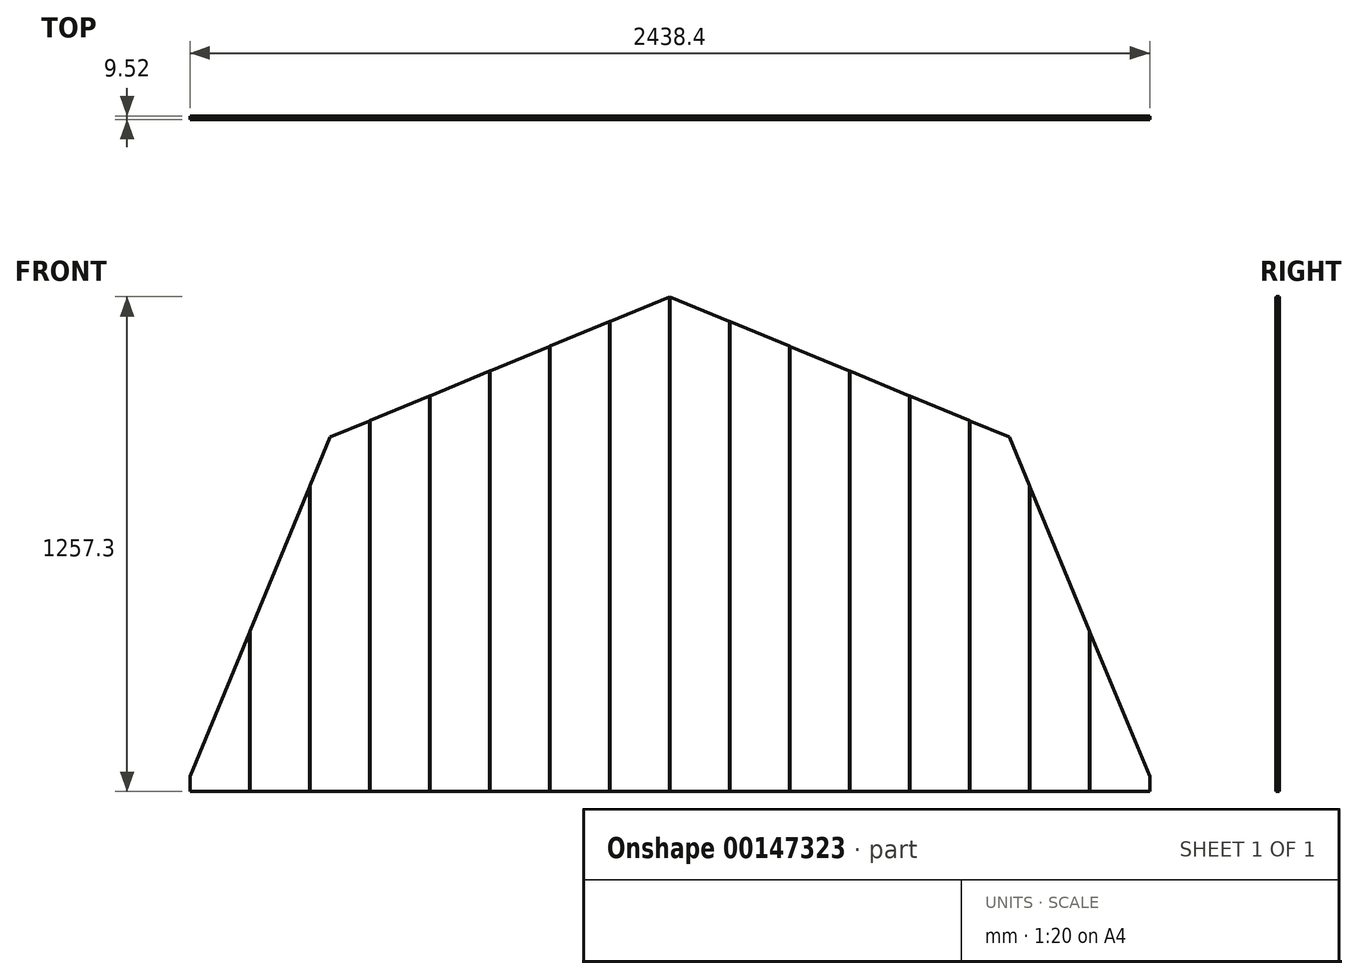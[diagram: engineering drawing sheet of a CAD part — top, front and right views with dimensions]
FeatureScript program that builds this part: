
annotation { "Feature Type Name" : "Feature", "Feature Type Description" : "" }
export const myFeature = defineFeature(function(context is Context, id is Id, definition is map)
    precondition{}
    {
        {
            var Q0;
            Q0=qCreatedBy(makeId("Front.planeOp"),FACE);
            var sketch = newSketch(context, id + "F0", { "sketchPlane" : qUnion([Q0])});
            skLineSegment(sketch, "E0", {"start": v(-1027.18, -196.14) * mm, "end": v(-670.66, 666.55) * mm});
            skLineSegment(sketch, "E1", {"start": v(-670.66, 666.55) * mm, "end": v(192.02, 1023.06) * mm});
            skLineSegment(sketch, "E2.MirrorCS", {"start": v(1411.22, -196.14) * mm, "end": v(1054.7, 666.55) * mm});
            skLineSegment(sketch, "E3.MirrorCS", {"start": v(1054.7, 666.55) * mm, "end": v(192.02, 1023.06) * mm});
            skLineSegment(sketch, "E4.top", {"start": v(-1027.18, -234.24) * mm, "end": v(1411.22, -234.24) * mm});
            skLineSegment(sketch, "E4.left", {"start": v(-1027.18, -196.14) * mm, "end": v(-1027.18, -234.24) * mm});
            skLineSegment(sketch, "E4.right", {"start": v(1411.22, -196.14) * mm, "end": v(1411.22, -234.24) * mm});
            skSolve(sketch);
        }
        {
            var Q0;
            Q0=qSketchRegion(id+"F0",true);
            extrude(context, id + "F1", {"entities" : qUnion([Q0]), "endBound" : BoundingType.SYMMETRIC, "depth" : 9.52 * mm});
        }
        {
            var Q0;
            Q0=makeQuery(id+"F1.opExtrude","SWEPT_FACE",FACE,{"disambiguationData":[OSD([sQuery(id+"F0.wireOp",EDGE,"E4.top")])]});
            var sketch = newSketch(context, id + "F2", { "sketchPlane" : qUnion([Q0])});
            skLineSegment(sketch, "E5.bottom", {"start": v(-875.57, 4.76) * mm, "end": v(-873.98, 4.76) * mm});
            skLineSegment(sketch, "E5.top", {"start": v(-875.57, 3.17) * mm, "end": v(-873.98, 3.17) * mm});
            skLineSegment(sketch, "E5.left", {"start": v(-875.57, 4.76) * mm, "end": v(-875.57, 3.17) * mm});
            skLineSegment(sketch, "E5.right", {"start": v(-873.98, 4.76) * mm, "end": v(-873.98, 3.17) * mm});
            skPoint(sketch, "E6.end.orphan", {"position": v(-874.78, 4.76) * mm});
            skPoint(sketch, "E6.start.orphan", {"position": v(-874.78, 3.17) * mm});
            skPoint(sketch, "E7.1.0.0", {"position": v(-722.38, 3.17) * mm});
            skPoint(sketch, "E7.1.0.1", {"position": v(-722.38, 4.76) * mm});
            skLineSegment(sketch, "E7.1.0.2", {"start": v(-723.17, 4.76) * mm, "end": v(-721.58, 4.76) * mm});
            skLineSegment(sketch, "E7.1.0.3", {"start": v(-723.17, 3.17) * mm, "end": v(-721.58, 3.17) * mm});
            skLineSegment(sketch, "E7.1.0.4", {"start": v(-723.17, 4.76) * mm, "end": v(-723.17, 3.17) * mm});
            skLineSegment(sketch, "E7.1.0.5", {"start": v(-721.58, 4.76) * mm, "end": v(-721.58, 3.17) * mm});
            skPoint(sketch, "E7.2.0.0", {"position": v(-569.98, 3.17) * mm});
            skPoint(sketch, "E7.2.0.1", {"position": v(-569.98, 4.76) * mm});
            skLineSegment(sketch, "E7.2.0.2", {"start": v(-570.77, 4.76) * mm, "end": v(-569.18, 4.76) * mm});
            skLineSegment(sketch, "E7.2.0.3", {"start": v(-570.77, 3.17) * mm, "end": v(-569.18, 3.17) * mm});
            skLineSegment(sketch, "E7.2.0.4", {"start": v(-570.77, 4.76) * mm, "end": v(-570.77, 3.17) * mm});
            skLineSegment(sketch, "E7.2.0.5", {"start": v(-569.18, 4.76) * mm, "end": v(-569.18, 3.17) * mm});
            skPoint(sketch, "E7.3.0.0", {"position": v(-417.58, 3.17) * mm});
            skPoint(sketch, "E7.3.0.1", {"position": v(-417.58, 4.76) * mm});
            skLineSegment(sketch, "E7.3.0.2", {"start": v(-418.37, 4.76) * mm, "end": v(-416.78, 4.76) * mm});
            skLineSegment(sketch, "E7.3.0.3", {"start": v(-418.37, 3.17) * mm, "end": v(-416.78, 3.17) * mm});
            skLineSegment(sketch, "E7.3.0.4", {"start": v(-418.37, 4.76) * mm, "end": v(-418.37, 3.17) * mm});
            skLineSegment(sketch, "E7.3.0.5", {"start": v(-416.78, 4.76) * mm, "end": v(-416.78, 3.17) * mm});
            skPoint(sketch, "E7.4.0.0", {"position": v(-265.18, 3.17) * mm});
            skPoint(sketch, "E7.4.0.1", {"position": v(-265.18, 4.76) * mm});
            skLineSegment(sketch, "E7.4.0.2", {"start": v(-265.97, 4.76) * mm, "end": v(-264.38, 4.76) * mm});
            skLineSegment(sketch, "E7.4.0.3", {"start": v(-265.97, 3.17) * mm, "end": v(-264.38, 3.17) * mm});
            skLineSegment(sketch, "E7.4.0.4", {"start": v(-265.97, 4.76) * mm, "end": v(-265.97, 3.17) * mm});
            skLineSegment(sketch, "E7.4.0.5", {"start": v(-264.38, 4.76) * mm, "end": v(-264.38, 3.17) * mm});
            skPoint(sketch, "E7.5.0.0", {"position": v(-112.78, 3.17) * mm});
            skPoint(sketch, "E7.5.0.1", {"position": v(-112.78, 4.76) * mm});
            skLineSegment(sketch, "E7.5.0.2", {"start": v(-113.57, 4.76) * mm, "end": v(-111.98, 4.76) * mm});
            skLineSegment(sketch, "E7.5.0.3", {"start": v(-113.57, 3.17) * mm, "end": v(-111.98, 3.17) * mm});
            skLineSegment(sketch, "E7.5.0.4", {"start": v(-113.57, 4.76) * mm, "end": v(-113.57, 3.17) * mm});
            skLineSegment(sketch, "E7.5.0.5", {"start": v(-111.98, 4.76) * mm, "end": v(-111.98, 3.17) * mm});
            skPoint(sketch, "E7.6.0.0", {"position": v(39.62, 3.17) * mm});
            skPoint(sketch, "E7.6.0.1", {"position": v(39.62, 4.76) * mm});
            skLineSegment(sketch, "E7.6.0.2", {"start": v(38.83, 4.76) * mm, "end": v(40.42, 4.76) * mm});
            skLineSegment(sketch, "E7.6.0.3", {"start": v(38.83, 3.17) * mm, "end": v(40.42, 3.17) * mm});
            skLineSegment(sketch, "E7.6.0.4", {"start": v(38.83, 4.76) * mm, "end": v(38.83, 3.17) * mm});
            skLineSegment(sketch, "E7.6.0.5", {"start": v(40.42, 4.76) * mm, "end": v(40.42, 3.17) * mm});
            skPoint(sketch, "E7.7.0.0", {"position": v(192.02, 3.17) * mm});
            skPoint(sketch, "E7.7.0.1", {"position": v(192.02, 4.76) * mm});
            skLineSegment(sketch, "E7.7.0.2", {"start": v(191.23, 4.76) * mm, "end": v(192.82, 4.76) * mm});
            skLineSegment(sketch, "E7.7.0.3", {"start": v(191.23, 3.17) * mm, "end": v(192.82, 3.17) * mm});
            skLineSegment(sketch, "E7.7.0.4", {"start": v(191.23, 4.76) * mm, "end": v(191.23, 3.17) * mm});
            skLineSegment(sketch, "E7.7.0.5", {"start": v(192.82, 4.76) * mm, "end": v(192.82, 3.17) * mm});
            skPoint(sketch, "E7.8.0.0", {"position": v(344.42, 3.17) * mm});
            skPoint(sketch, "E7.8.0.1", {"position": v(344.42, 4.76) * mm});
            skLineSegment(sketch, "E7.8.0.2", {"start": v(343.63, 4.76) * mm, "end": v(345.22, 4.76) * mm});
            skLineSegment(sketch, "E7.8.0.3", {"start": v(343.63, 3.17) * mm, "end": v(345.22, 3.17) * mm});
            skLineSegment(sketch, "E7.8.0.4", {"start": v(343.63, 4.76) * mm, "end": v(343.63, 3.17) * mm});
            skLineSegment(sketch, "E7.8.0.5", {"start": v(345.22, 4.76) * mm, "end": v(345.22, 3.17) * mm});
            skPoint(sketch, "E7.9.0.0", {"position": v(496.82, 3.17) * mm});
            skPoint(sketch, "E7.9.0.1", {"position": v(496.82, 4.76) * mm});
            skLineSegment(sketch, "E7.9.0.2", {"start": v(496.03, 4.76) * mm, "end": v(497.62, 4.76) * mm});
            skLineSegment(sketch, "E7.9.0.3", {"start": v(496.03, 3.17) * mm, "end": v(497.62, 3.17) * mm});
            skLineSegment(sketch, "E7.9.0.4", {"start": v(496.03, 4.76) * mm, "end": v(496.03, 3.17) * mm});
            skLineSegment(sketch, "E7.9.0.5", {"start": v(497.62, 4.76) * mm, "end": v(497.62, 3.17) * mm});
            skPoint(sketch, "E7.10.0.0", {"position": v(649.22, 3.17) * mm});
            skPoint(sketch, "E7.10.0.1", {"position": v(649.22, 4.76) * mm});
            skLineSegment(sketch, "E7.10.0.2", {"start": v(648.43, 4.76) * mm, "end": v(650.02, 4.76) * mm});
            skLineSegment(sketch, "E7.10.0.3", {"start": v(648.43, 3.17) * mm, "end": v(650.02, 3.17) * mm});
            skLineSegment(sketch, "E7.10.0.4", {"start": v(648.43, 4.76) * mm, "end": v(648.43, 3.17) * mm});
            skLineSegment(sketch, "E7.10.0.5", {"start": v(650.02, 4.76) * mm, "end": v(650.02, 3.17) * mm});
            skPoint(sketch, "E7.11.0.0", {"position": v(801.62, 3.17) * mm});
            skPoint(sketch, "E7.11.0.1", {"position": v(801.62, 4.76) * mm});
            skLineSegment(sketch, "E7.11.0.2", {"start": v(800.83, 4.76) * mm, "end": v(802.42, 4.76) * mm});
            skLineSegment(sketch, "E7.11.0.3", {"start": v(800.83, 3.17) * mm, "end": v(802.42, 3.17) * mm});
            skLineSegment(sketch, "E7.11.0.4", {"start": v(800.83, 4.76) * mm, "end": v(800.83, 3.17) * mm});
            skLineSegment(sketch, "E7.11.0.5", {"start": v(802.42, 4.76) * mm, "end": v(802.42, 3.17) * mm});
            skPoint(sketch, "E7.12.0.0", {"position": v(954.02, 3.17) * mm});
            skPoint(sketch, "E7.12.0.1", {"position": v(954.02, 4.76) * mm});
            skLineSegment(sketch, "E7.12.0.2", {"start": v(953.23, 4.76) * mm, "end": v(954.82, 4.76) * mm});
            skLineSegment(sketch, "E7.12.0.3", {"start": v(953.23, 3.17) * mm, "end": v(954.82, 3.17) * mm});
            skLineSegment(sketch, "E7.12.0.4", {"start": v(953.23, 4.76) * mm, "end": v(953.23, 3.17) * mm});
            skLineSegment(sketch, "E7.12.0.5", {"start": v(954.82, 4.76) * mm, "end": v(954.82, 3.17) * mm});
            skPoint(sketch, "E7.13.0.0", {"position": v(1106.42, 3.17) * mm});
            skPoint(sketch, "E7.13.0.1", {"position": v(1106.42, 4.76) * mm});
            skLineSegment(sketch, "E7.13.0.2", {"start": v(1105.63, 4.76) * mm, "end": v(1107.22, 4.76) * mm});
            skLineSegment(sketch, "E7.13.0.3", {"start": v(1105.63, 3.17) * mm, "end": v(1107.22, 3.17) * mm});
            skLineSegment(sketch, "E7.13.0.4", {"start": v(1105.63, 4.76) * mm, "end": v(1105.63, 3.17) * mm});
            skLineSegment(sketch, "E7.13.0.5", {"start": v(1107.22, 4.76) * mm, "end": v(1107.22, 3.17) * mm});
            skPoint(sketch, "E7.14.0.0", {"position": v(1258.82, 3.17) * mm});
            skPoint(sketch, "E7.14.0.1", {"position": v(1258.82, 4.76) * mm});
            skLineSegment(sketch, "E7.14.0.2", {"start": v(1258.03, 4.76) * mm, "end": v(1259.62, 4.76) * mm});
            skLineSegment(sketch, "E7.14.0.3", {"start": v(1258.03, 3.17) * mm, "end": v(1259.62, 3.17) * mm});
            skLineSegment(sketch, "E7.14.0.4", {"start": v(1258.03, 4.76) * mm, "end": v(1258.03, 3.17) * mm});
            skLineSegment(sketch, "E7.14.0.5", {"start": v(1259.62, 4.76) * mm, "end": v(1259.62, 3.17) * mm});
            skLineSegment(sketch, "E7.direction1", {"start": v(-874.78, 3.17) * mm, "end": v(-722.38, 3.17) * mm, "construction": true});
            skSolve(sketch);
        }
        {
            var Q0;
            Q0=qSketchRegion(id+"F2",true);
            extrude(context, id + "F3", {"entities" : qUnion([Q0]), "operationType" : NewBodyOperationType.REMOVE, "endBound" : BoundingType.THROUGH_ALL, "oppositeDirection" : true, "depth" : 25.4 * mm});
        }
    });
